# Revit family: NLRS_27_GM_LIB_V28_MR
name_source: partatom
category: Generic Models
revit_build: Autodesk Revit 2017 (Build: 20160225_1515(x64)
units: mm (PartAtom-declared; Revit-internal decimal feet)

## family parameters
Can host rebar = No
Cut with Voids When Loaded = No
Part Type = Normal
Room Calculation Point = No
Round Connector Dimension = Use Diameter
Shared = No

## types (5) — shared parameters
Assembly Code = 27.16
Dakhelling = 40.00°
Description = Beugel goot type V28
Graden beugel = 50.00°
IfcExportAs = IfcFlowSegment
Manufacturer = Meilof Riks
Model = V28
NLRS_C_content_datum_uitgifte = 21-12-2018
Set_Condition_L = Goot_profiel_GM_LIB_L_H_eind
Set_Condition_R = Goot_profiel_GM_LIB_R_H_eind
URL = https://www.meilofriks.nl
set_beugeltype = V28 - beugel_G

## per-type parameters (varying)
| type | Kleur | NLRS_C_materiaal |
| RAL 7016 | antraciet (RAL7016) | RAL 7016 |
| RAL 7036 | grijs (RAL7036) | RAL 7036 |
| RAL 9001 | crème (RAL9001) | RAL 9001 |
| RAL 9006 | zilver (RAL9006) | RAL 9006 |
| WIT AC 1382 ≈ RAL 9016 | wit (AC1382) | RAL 9016 |

## geometry (parser evidence)
native form markers: Sweep x34
no freeform markers — native parametric forms only
